# Revit family: Tables-Teknion-BCGRLB_Rectangular_Writable_Glass_Meeting_Blade_Legs-R2018
name_source: partatom
category: Furniture
revit_build: Autodesk Revit 2018 (Build: 20190510_1515(x64)
units: mm (PartAtom-declared; Revit-internal decimal feet)

## family parameters
Always vertical = Yes
Cut with Voids When Loaded = No
OmniClass Number = 23.40.20.00
OmniClass Title = General Furniture and Specialties
Room Calculation Point = No
Shared = Yes
Work Plane-Based = No

## types (5) — shared parameters
Assembly Code = E2020200
Manufacturer = Teknion
Manufacturer Fax = 416.661.4586
Part Number = BCGRLB
Product Documentation Link = https://www.teknion.com
Product Line = Expansion Casegoods
Product Page URL = https://www.teknion.com
Series = Expansion Casegoods
Sustainability Data = https://www.teknion.com
URL = www.teknion.com
Unit Weight URL = http://www.teknion.com
Warranty = http://www.teknion.com

## per-type parameters (varying)
| type | Description | Model | Width |
| 96" Width, With Companion Marker Kit | Rectangular Writable Glass Meeting Table - Blade Legs, 96 inch Width, With Companion Kit | BCGRLB__96__K | 95.52 " |
| 90" Width, With Companion Market Kit | Rectangular Writable Glass Meeting Table - Blade Legs, 90 inch Width, With Companion Kit | BCGRLB__90__K | 89.55 " |
| 84" Width, With Companion Market Kit | Rectangular Writable Glass Meeting Table - Blade Legs, 84 inch Width, With Companion Kit | BCGRLB__84__K | 83.58 " |
| 78" Width, With Companion Market Kit | Rectangular Writable Glass Meeting Table - Blade Legs, 78 inch Width, With Companion Kit | BCGRLB__78__K | 77.61 " |
| 72" Width, With Companion Market Kit | Rectangular Writable Glass Meeting Table - Blade Legs, 72 inch Width, With Companion Kit | BCGRLB__72__K | 71.64 " |

## geometry (parser evidence)
native form markers: Sweep x5
no freeform markers — native parametric forms only
